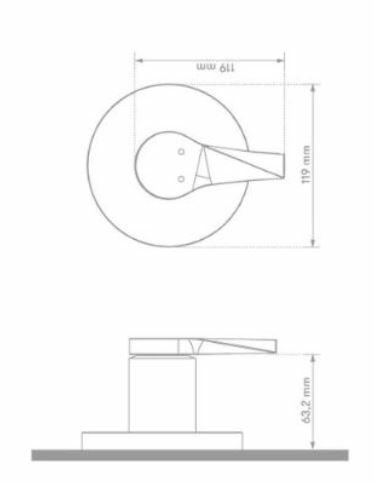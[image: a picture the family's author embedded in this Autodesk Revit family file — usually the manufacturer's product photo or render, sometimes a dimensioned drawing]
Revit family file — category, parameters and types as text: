
# Revit family: 01-1133-00-LLAVE DUCHA KRISTHAL
name_source: partatom
category: Aparatos sanitarios
revit_build: Autodesk Revit 2018 (Build: 20170223_1515(x64)
units: mm (PartAtom-declared; Revit-internal decimal feet)

## family parameters
Anfitrión = Cara
Compartido = No
Corte con vacíos al cargar = No
Cota de conector redondo = Diámetro de uso
Número OmniClass = 23.31.11.00
Punto de cálculo de habitación = No
Tipo de pieza = Normal

## types (1)
- 01-1133-00
    Alto = 70.5 mm
    Ancho = 60.2 mm  [stored 0.197507 ft]
    Conexión AC = Sí
    Conexión AF = Sí
    Conexión de residuos = No
    Conexión de ventilación = No
    Descripción = Registro ducha
    Elevación por defecto = 0 mm  [stored 0 ft]
    Fabricante = Gricol
    Imagen de tipo = <Ninguno>
    Link Ficha Tecnica = http://infotecnica.gricol.com
    Modelo = 01-1133-00
    Plastico ABS Cromado = Plastico ABS Cromado
    Plastico Acrilico Transparente = Plastico Acrilico Transparente
    Product Name = REGISTRO KRISTHAL
    Profundidad = 65.6 mm  [stored 0.215223 ft]
    URL = https://www.gricol.com

note: [stored X ft] marks values corroborated as IEEE doubles in the binary element streams (Revit-internal decimal feet)

## geometry (parser evidence)
native form markers: Blend x4, Sweep x5
no freeform markers — native parametric forms only
